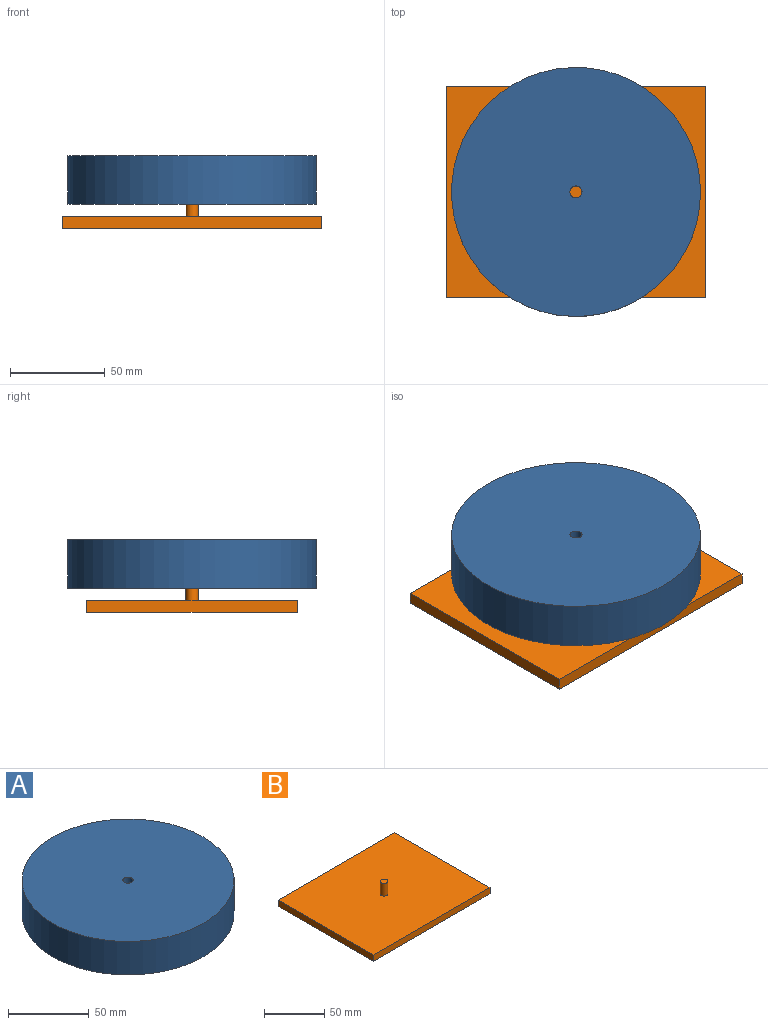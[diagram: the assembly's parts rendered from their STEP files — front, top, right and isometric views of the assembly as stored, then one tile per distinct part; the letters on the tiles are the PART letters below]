
ASSEMBLY  parts=2 mates=1
PART A: 4 faces, bbox 131.4x131.4x25.4 mm
  f0: cylinder r=3.17mm len=25.4mm, axis (0,0,-1), area 506.7mm2, adj f2,f3
  f1: cylinder r=65.71mm len=131.42mm, axis (0,0,-1), area 10486.7mm2, adj f2,f3
  f2: plane 131.42x131.42mm, normal (0,0,1), area 13532.8mm2, adj f0,f1
  f3: plane 131.42x131.42mm, normal (0,0,-1), area 13532.8mm2, adj f0,f1
PART B: 8 faces, bbox 136.6x111.3x19.1 mm
  f0: plane 136.56x6.35mm, normal (0,1,0), area 867.1mm2, adj f1,f3,f4,f5
  f1: plane 111.32x6.35mm, normal (-1,0,0), area 706.9mm2, adj f0,f2,f4,f5
  f2: plane 136.56x6.35mm, normal (0,-1,0), area 867.1mm2, adj f1,f3,f4,f5
  f3: plane 111.32x6.35mm, normal (1,0,0), area 706.9mm2, adj f0,f2,f4,f5
  f4: plane 136.56x111.32mm, normal (0,0,-1), area 15201.5mm2, adj f0,f1,f2,f3
  f5: plane 136.56x111.32mm, normal (0,0,1), area 15169.8mm2, adj f0,f1,f2,f3,f6
  f6: cylinder r=3.17mm len=12.7mm, axis (0,0,-1), area 253.4mm2, adj f5,f7
  f7: plane 6.35x6.35mm, normal (0,0,1), area 31.7mm2, adj f6
PLACE A t=(-95.56,-56.46,6.29)mm
PLACE B t=(-95.56,-56.46,-0.06)mm
MATE pin_slot B.f6 <-> A.f0  axis (0,0,-1) through (-95.56,-56.46,6.29)mm
